# Revit family: NBS_DudleyIndustries_SoapDpnsrs_BehindTheMirrorRange_LiquidSoapDispenser0-4Litre
name_source: partatom
category: Generic Models
revit_build: Autodesk Revit 2016 (Build: 20150220_1215(x64)
units: mm (PartAtom-declared; Revit-internal decimal feet)

## family parameters
Can host rebar = No
Cut with Voids When Loaded = No
Host = Face
OmniClass Number = 23.40.20.21.34
OmniClass Title = Soap Holders, Dispensers
Part Type = Normal
Room Calculation Point = No
Round Connector Dimension = Use Diameter
Shared = No

## types (1)
- BehindTheMirrorRangeLiquidSoapDispenser0-4Litre
    AssetType = Fixed
    BIMObjectName = NBS_DudleyIndustries_SoapDispensers_BehindtheMirrorRange_LiquidSoapdispenser0-4litre
    Category = Pr_40_70_22_81:Soap dispensers
    Default Elevation = 1200 mm
    Description = Lever operated ‘Behind the Mirror’ 0.4 litre liquid Soap Dispenser
    DispenserCaseMaterial = NBS_Concept
    DispenserLevelMaterial = NBS_Concept
    DurationUnit = year
    ExpectedLife = 5
    Finish = Brushed
    Form = Fixed in line with base of cabinet
    IfcExportAs = IfcFurnitureType
    IfcExportType = NOTDEFINED
    MainColor = Stainless Steel
    ManufacturerName = Dudley Industries
    ManufacturerURL = www.dudleyindustries.com/
    Material = Stainless Steel
    MaterialsBody = Stainless Steel
    MaterialsFinishColour = Brushed
    ModelNumber = 92020
    ModelReference = Behind the Mirror Range: Liquid Soap dispenser 0.4 litre
    NBSCertification = www.nationalbimlibrary.com/cert/q4tkfio1
    NBSDescription = Soap dispensers
    NBSReference = 45-35-72/358
    Name = SoapDispensers_BehindTheMirrorRange_LiquidSoapdispenser0-4litre_DudleyIndustries
    NominalDepth = 120 mm  [stored 0.393701 ft]
    NominalHeight = 250 mm  [stored 0.82021 ft]
    NominalLength = 110 mm  [stored 0.360892 ft]
    NominalWidth = 110 mm  [stored 0.360892 ft]
    Operation = Manual pull lever operation
    ProductInformation = www.dudleyindustries.com/wp-content/uploads/2016/11/0.4-Litre-Liquid-Soap-Dispenser.pdf
    Size = 212 x H.343 x 160 mm
    Style = Soap dispenser
    Uniclass2015Code = Pr_40_70_22_81
    Uniclass2015Title = Soap dispensers
    Uniclass2015Version = Products v1.7
    Version = 2
    WarrantyDescription = 1 year warranty
    WarrantyDurationParts = 1
    WarrantyDurationUnit = year

note: [stored X ft] marks values corroborated as IEEE doubles in the binary element streams (Revit-internal decimal feet)

## geometry (parser evidence)
native form markers: Sweep x2
no freeform markers — native parametric forms only
